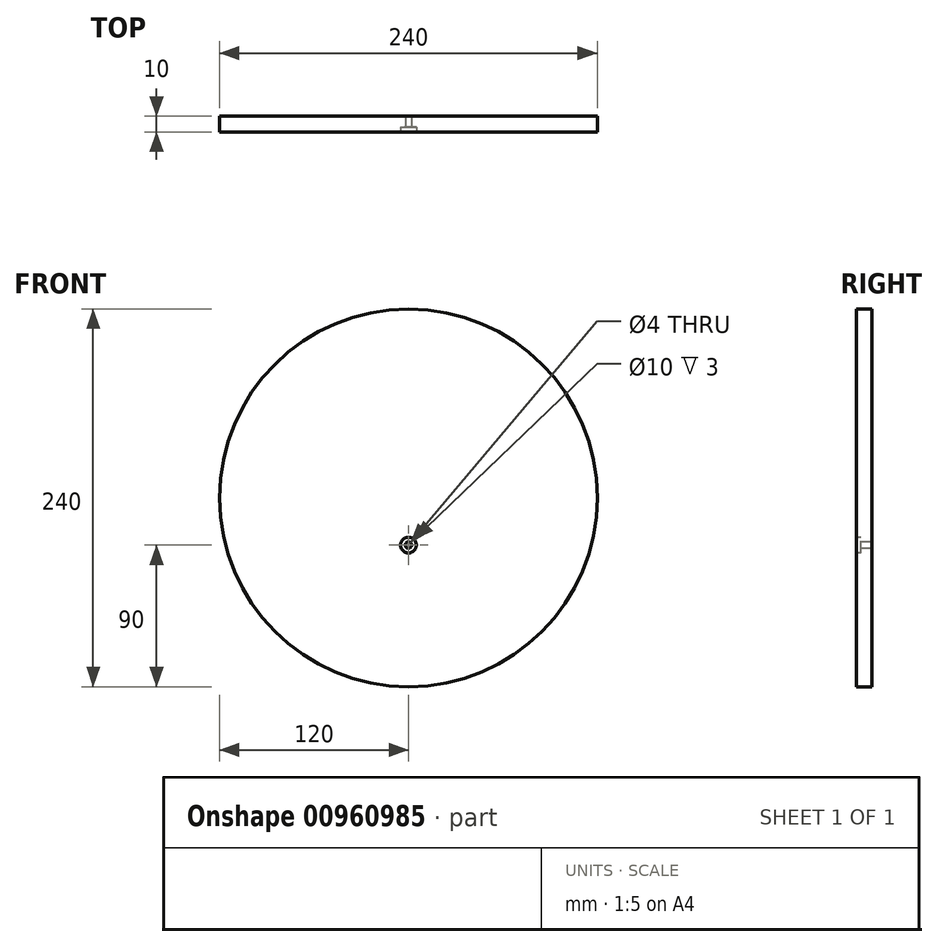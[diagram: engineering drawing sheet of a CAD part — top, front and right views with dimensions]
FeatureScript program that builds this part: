
annotation { "Feature Type Name" : "Feature", "Feature Type Description" : "" }
export const myFeature = defineFeature(function(context is Context, id is Id, definition is map)
    precondition{}
    {
        {
            var Q0;
            Q0=qCreatedBy(makeId("Front.planeOp"),FACE);
            var sketch = newSketch(context, id + "F0", { "sketchPlane" : qUnion([Q0])});
            skCircle(sketch, "E0", {"center": v(0, 0) * mm, "radius": 120 * mm});
            skLineSegment(sketch, "E1", {"start": v(0, 0) * mm, "end": v(0, -110) * mm, "construction": true});
            skLineSegment(sketch, "E2", {"start": v(0, -110) * mm, "end": v(-40, -110) * mm, "construction": true});
            skLineSegment(sketch, "E3", {"start": v(-40, -110) * mm, "end": v(-40, -80) * mm, "construction": true});
            skLineSegment(sketch, "E4", {"start": v(-40, -95) * mm, "end": v(-60, -95) * mm, "construction": true});
            skLineSegment(sketch, "E5", {"start": v(0, 0) * mm, "end": v(0, -30) * mm, "construction": true});
            skCircle(sketch, "E6", {"center": v(0, -30) * mm, "radius": 2 * mm});
            skSolve(sketch);
        }
        {
            var Q0;
            Q0 = qSketchRegion(id + "F0", true);
            extrude(context, id + "F1", {"entities" : qUnion([Q0]), "oppositeDirection" : true, "depth" : 10 * mm, "offsetDistance" : 25 * mm});
        }
        {
            var Q0;
            Q0=qCreatedBy(makeId("Front.planeOp"),FACE);
            var sketch = newSketch(context, id + "F2", { "sketchPlane" : qUnion([Q0])});
            skLineSegment(sketch, "E7", {"start": v(0, 0) * mm, "end": v(0, -110) * mm, "construction": true});
            skLineSegment(sketch, "E8", {"start": v(0, -110) * mm, "end": v(-40, -110) * mm, "construction": true});
            skLineSegment(sketch, "E9", {"start": v(-40, -110) * mm, "end": v(-40, -95) * mm, "construction": true});
            skLineSegment(sketch, "E10", {"start": v(-40, -95) * mm, "end": v(-60, -95) * mm, "construction": true});
            skLineSegment(sketch, "E11", {"start": v(0, 0) * mm, "end": v(0, -30) * mm, "construction": true});
            skCircle(sketch, "E12", {"center": v(0, -30) * mm, "radius": 5 * mm});
            skSolve(sketch);
        }
        {
            var Q0;
            Q0 = qSketchRegion(id + "F2", true);
            extrude(context, id + "F3", {"entities" : qUnion([Q0]), "operationType" : NewBodyOperationType.REMOVE, "oppositeDirection" : true, "depth" : 3 * mm, "offsetDistance" : 25 * mm});
        }
    });
